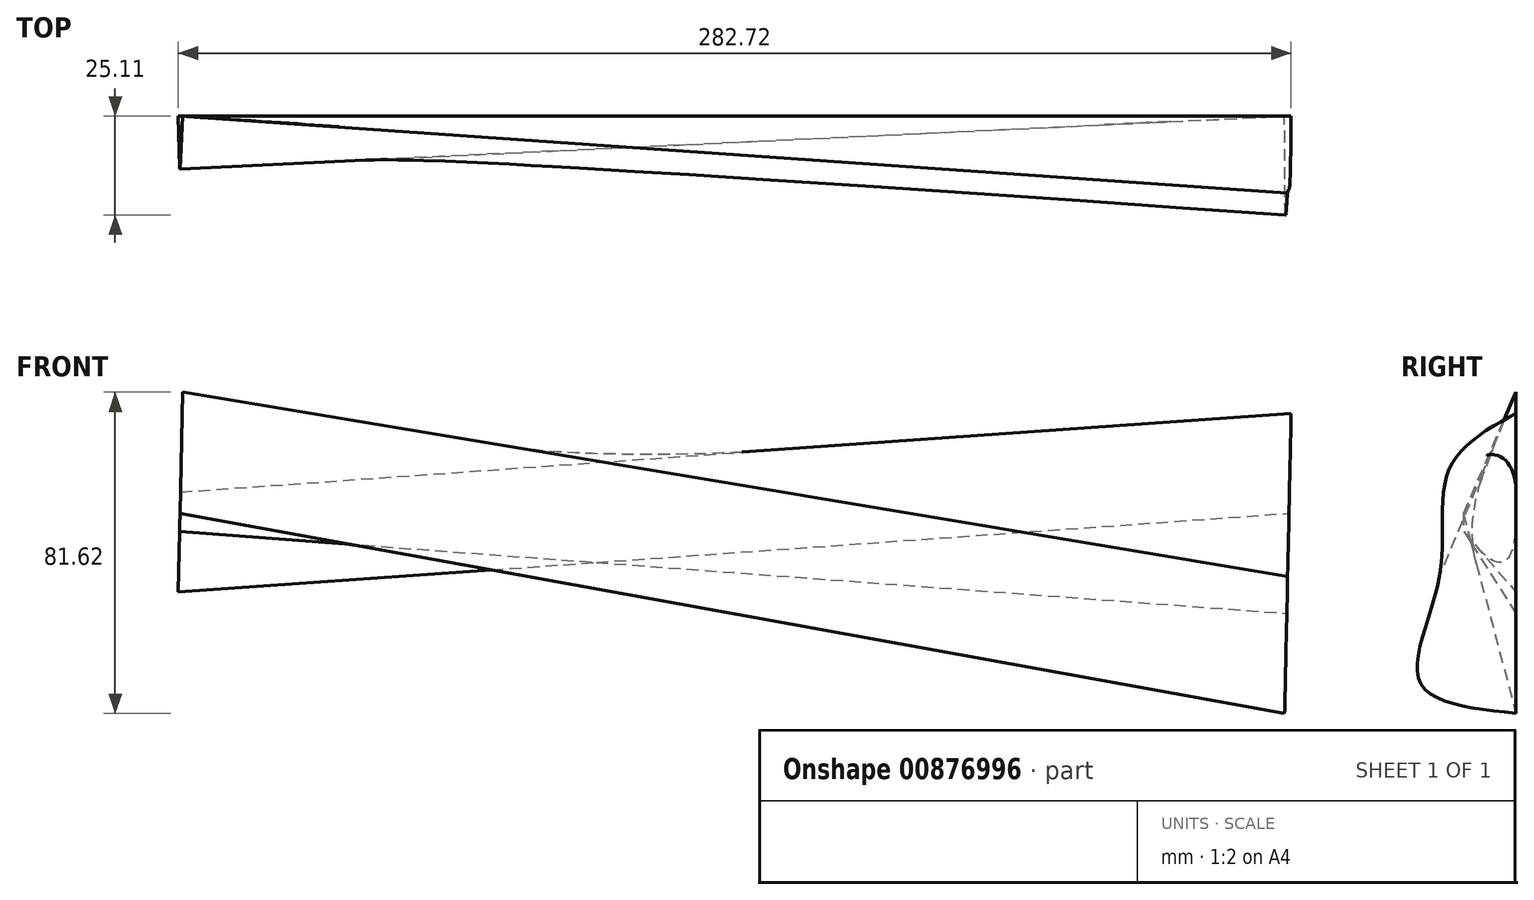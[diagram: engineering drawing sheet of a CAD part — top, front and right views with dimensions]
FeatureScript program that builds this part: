
annotation { "Feature Type Name" : "Feature", "Feature Type Description" : "" }
export const myFeature = defineFeature(function(context is Context, id is Id, definition is map)
    precondition{}
    {
        {
            var Q0;
            Q0=qCreatedBy(makeId("Front.planeOp"),FACE);
            var sketch = newSketch(context, id + "F0", { "sketchPlane" : qUnion([Q0])});
            skCircle(sketch, "E0", {"center": v(0, 0) * mm, "radius": 21 * mm});
            skSolve(sketch);
        }
        {
            var Q0;
            Q0=qCreatedBy(makeId("Front.planeOp"),FACE);
            var sketch = newSketch(context, id + "F1", { "sketchPlane" : qUnion([Q0])});
            skLineSegment(sketch, "E1", {"start": v(0, 0) * mm, "end": v(0, 75) * mm, "construction": true});
            skLineSegment(sketch, "E2", {"start": v(0, 75) * mm, "end": v(-443.7, 75) * mm});
            skLineSegment(sketch, "E3", {"start": v(0, 0) * mm, "end": v(-443.7, 75) * mm});
            skLineSegment(sketch, "E4", {"start": v(0, 75) * mm, "end": v(556.3, 75) * mm});
            skCircle(sketch, "E5", {"center": v(556.3, 75) * mm, "radius": 340 * mm});
            skCircle(sketch, "E6", {"center": v(-443.7, 75) * mm, "radius": 340 * mm});
            skLineSegment(sketch, "E7", {"start": v(0, 0) * mm, "end": v(0, -265) * mm, "construction": true});
            skLineSegment(sketch, "E8", {"start": v(0, -265) * mm, "end": v(1141.2, -265) * mm, "construction": true});
            skLineSegment(sketch, "E9", {"start": v(0, -265) * mm, "end": v(-741.23, -265) * mm, "construction": true});
            skPoint(sketch, "E10", {"position": v(925.16, -265) * mm});
            skLineSegment(sketch, "E11", {"start": v(925.16, -265) * mm, "end": v(925.16, 565) * mm, "construction": true});
            skPoint(sketch, "E12", {"position": v(-183.96, -265) * mm});
            skLineSegment(sketch, "E13", {"start": v(-183.96, -265) * mm, "end": v(-183.96, 435) * mm, "construction": true});
            skLineSegment(sketch, "E14", {"start": v(556.3, 75) * mm, "end": v(427.66, 495.77) * mm, "construction": true});
            skLineSegment(sketch, "E15", {"start": v(0, -59.9) * mm, "end": v(66.47, -31.2) * mm});
            skLineSegment(sketch, "E16", {"start": v(66.47, -31.2) * mm, "end": v(198.5, 169.22) * mm});
            skLineSegment(sketch, "E17", {"start": v(227.37, 161.04) * mm, "end": v(198.5, 169.22) * mm, "construction": true});
            skLineSegment(sketch, "E18", {"start": v(309.98, 309.36) * mm, "end": v(289.2, 331) * mm, "construction": true});
            skLineSegment(sketch, "E19", {"start": v(397.94, 375.87) * mm, "end": v(385.1, 402.98) * mm, "construction": true});
            skArc(sketch, "E20", {"start": v(385.1, 402.98) * mm, "mid": v(267.14, 305.8) * mm, "end": v(198.5, 169.22) * mm});
            skLineSegment(sketch, "E21", {"start": v(427.66, 495.77) * mm, "end": v(383.8, 639.22) * mm});
            skLineSegment(sketch, "E22", {"start": v(385.1, 402.98) * mm, "end": v(392.65, 448.48) * mm});
            skLineSegment(sketch, "E23", {"start": v(392.65, 448.48) * mm, "end": v(401.41, 479.68) * mm});
            skLineSegment(sketch, "E24", {"start": v(401.41, 479.68) * mm, "end": v(427.66, 495.77) * mm});
            skLineSegment(sketch, "E25", {"start": v(383.8, 639.22) * mm, "end": v(356.98, 631.02) * mm});
            skLineSegment(sketch, "E26", {"start": v(383.8, 639.22) * mm, "end": v(410.18, 647.29) * mm});
            skLineSegment(sketch, "E27", {"start": v(427.66, 495.77) * mm, "end": v(452.73, 503.44) * mm});
            skLineSegment(sketch, "E28", {"start": v(410.18, 647.29) * mm, "end": v(452.73, 503.44) * mm});
            skLineSegment(sketch, "E29", {"start": v(356.98, 631.02) * mm, "end": v(401.41, 479.68) * mm});
            skLineSegment(sketch, "E30", {"start": v(356.98, 631.02) * mm, "end": v(324.22, 639.05) * mm});
            skLineSegment(sketch, "E31", {"start": v(324.22, 639.05) * mm, "end": v(252.28, 613.05) * mm});
            skLineSegment(sketch, "E32", {"start": v(252.28, 613.05) * mm, "end": v(165.4, 593.75) * mm});
            skLineSegment(sketch, "E33", {"start": v(165.4, 593.75) * mm, "end": v(-116.2, 599.85) * mm});
            skLineSegment(sketch, "E34", {"start": v(383.8, 639.22) * mm, "end": v(-116.2, 639.22) * mm, "construction": true});
            skLineSegment(sketch, "E35", {"start": v(-116.2, 639.22) * mm, "end": v(-116.2, 599.85) * mm, "construction": true});
            skPoint(sketch, "E36", {"position": v(147.96, 92.5) * mm});
            skLineSegment(sketch, "E37", {"start": v(-23.84, 597.84) * mm, "end": v(-23.84, -265) * mm, "construction": true});
            skPoint(sketch, "E38.orphan", {"position": v(-116.2, 560.47) * mm});
            skSolve(sketch);
        }
        {
            var Q0;
            Q0=sQuery(id+"F1.wireOp",EDGE,"E33");
            var Q1;
            Q1=sQuery(id+"F1.wireOp",VERTEX,"E33.end");
            cPlane(context, id + "F2", {"entities" : qUnion([Q0, Q1]), "cplaneType" : CPlaneType.LINE_POINT, "offset" : 25.4 * mm, "width" : 152.4 * mm, "height" : 152.4 * mm});
        }
        {
            var Q0;
            Q0=qCreatedBy(id+"F2.planeOp",FACE);
            var sketch = newSketch(context, id + "F3", { "sketchPlane" : qUnion([Q0])});
            skLineSegment(sketch, "E39", {"start": v(0, 597.24) * mm, "end": v(0, 571.82) * mm});
            skLineSegment(sketch, "E40", {"start": v(0, 597.24) * mm, "end": v(0, 622.64) * mm});
            skFitSpline(sketch, "E41", {"points": [v(0, 622.64) * mm, v(10.72, 614.83) * mm, v(13.4, 591.78) * mm, v(10.1, 574.89) * mm, v(0, 571.82) * mm], "startDerivative": vector(54.82, -24.36) * mm, "endDerivative": vector(-57.3, -4.64) * mm});
            skLineSegment(sketch, "E42", {"start": v(13.24, 587.16) * mm, "end": v(0, 571.82) * mm});
            skLineSegment(sketch, "E43", {"start": v(0, 622.64) * mm, "end": v(13.4, 591.78) * mm});
            skSolve(sketch);
        }
        {
            var Q0;
            Q0=sQuery(id+"F1.wireOp",VERTEX,"E32.end");
            var Q1;
            Q1=sQuery(id+"F1.wireOp",EDGE,"E33");
            cPlane(context, id + "F4", {"entities" : qUnion([Q0, Q1]), "cplaneType" : CPlaneType.LINE_POINT, "offset" : 25.4 * mm, "width" : 152.4 * mm, "height" : 152.4 * mm});
        }
        {
            var Q0;
            Q0=qCreatedBy(id+"F4.planeOp",FACE);
            var sketch = newSketch(context, id + "F5", { "sketchPlane" : qUnion([Q0])});
            skPoint(sketch, "E44.start.orphan", {"position": v(0, 597.93) * mm});
            skLineSegment(sketch, "E45", {"start": v(0, 597.93) * mm, "end": v(0, 623.36) * mm});
            skLineSegment(sketch, "E46", {"start": v(0, 597.93) * mm, "end": v(0, 547.1) * mm});
            skFitSpline(sketch, "E47", {"points": [v(0, 623.36) * mm, v(16.9, 609.27) * mm, v(19.48, 581.86) * mm, v(24.38, 555.04) * mm, v(0, 547.1) * mm], "startDerivative": vector(91.43, -50.5) * mm, "endDerivative": vector(-129.9, -13.6) * mm});
            skSolve(sketch);
        }
        {
            var Q0;
            Q0=makeQuery(id+"F3.imprint","IMPRINT",FACE,{"disambiguationData":[TD([[makeQuery(id+"F3.imprint","IMPRINT",EDGE,{"derivedFrom":sQuery(id+"F3.wireOp",EDGE,"E39")}),1.0]])]});
            var Q1;
            Q1=makeQuery(id+"F5.imprint","IMPRINT",FACE,{"disambiguationData":[TD([[makeQuery(id+"F5.imprint","IMPRINT",EDGE,{"derivedFrom":sQuery(id+"F5.wireOp",EDGE,"E45")}),-1.0]])]});
            var Q2;
            Q2=sQuery(id+"F3.wireOp",VERTEX,"E41.start");
            var Q3;
            Q3=sQuery(id+"F5.wireOp",VERTEX,"E47.2.internal");
            loft(context, id + "F6", {"sheetProfilesArray" : [{ "sheetProfileEntities" : qUnion([Q0]) }, { "sheetProfileEntities" : qUnion([Q1]) }], "matchConnections" : true, "connections" : [{ "connectionEntities" : qUnion([Q2, Q3]), "connectionEdgeQueries" : qUnion([]), "connectionEdgeParameters" : [] }]});
        }
        {
            var Q0;
            Q0=sQuery(id+"F1.wireOp",EDGE,"E16");
            var Q1;
            Q1=sQuery(id+"F1.wireOp",VERTEX,"E15.end");
            cPlane(context, id + "F7", {"entities" : qUnion([Q0, Q1]), "cplaneType" : CPlaneType.LINE_POINT, "offset" : 25.4 * mm, "width" : 152.4 * mm, "height" : 152.4 * mm});
        }
        {
            var Q0;
            Q0=sQuery(id+"F0.wireOp",EDGE,"E0");
            extrude(context, id + "F8", {"bodyType" : ToolBodyType.SURFACE, "surfaceEntities" : qUnion([Q0]), "endBound" : BoundingType.SYMMETRIC, "depth" : 75 * mm, "offsetDistance" : 25.4 * mm});
        }
    });
